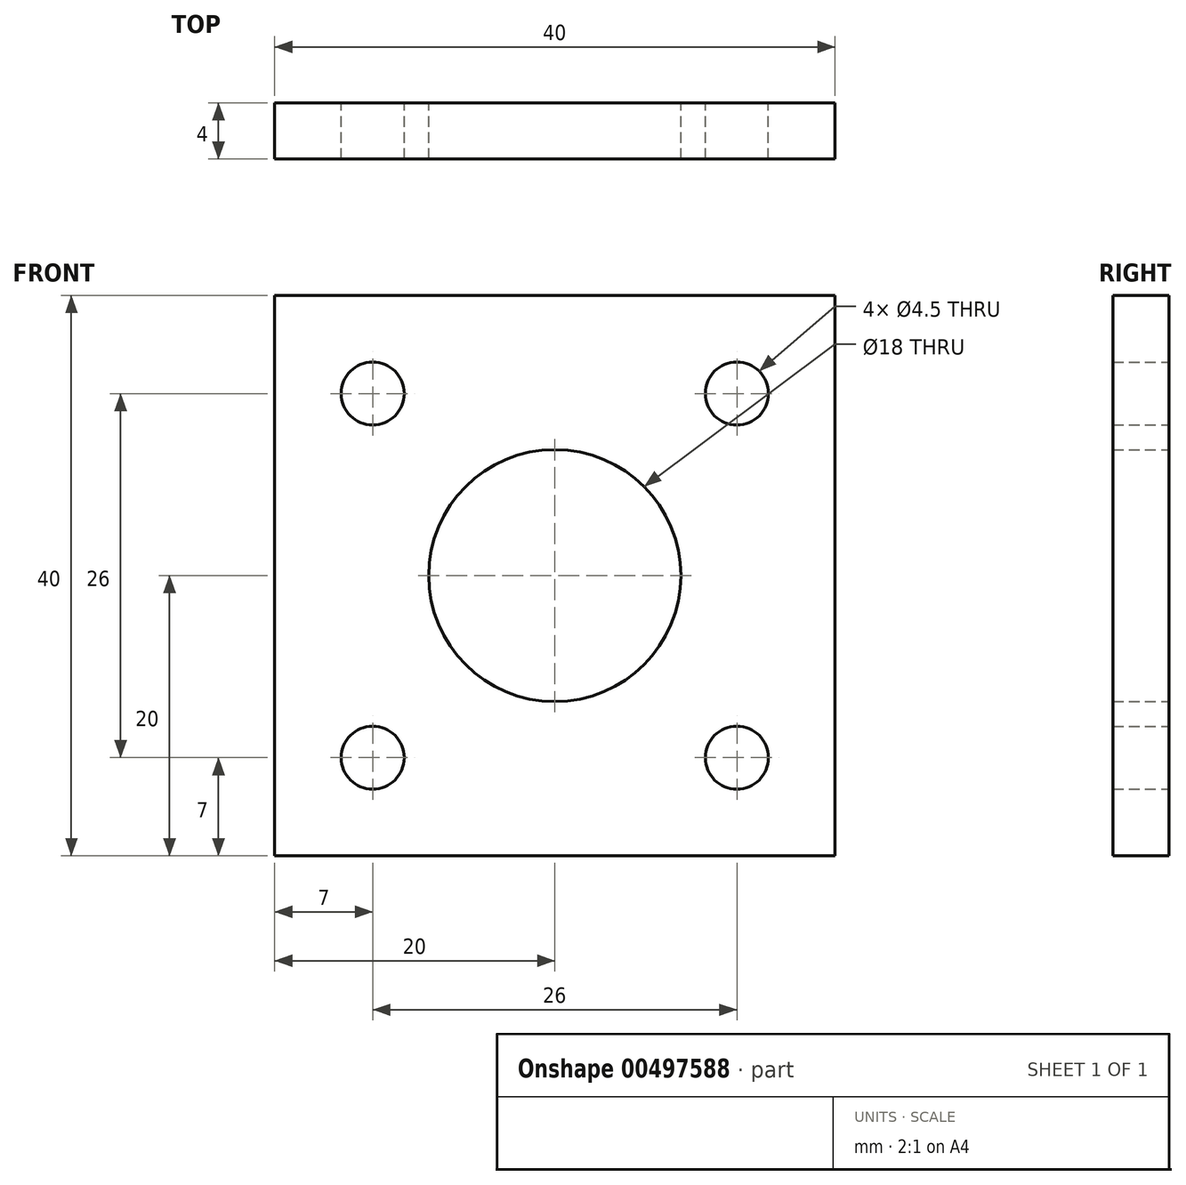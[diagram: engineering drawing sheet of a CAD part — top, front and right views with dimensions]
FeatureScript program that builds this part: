
annotation { "Feature Type Name" : "Feature", "Feature Type Description" : "" }
export const myFeature = defineFeature(function(context is Context, id is Id, definition is map)
    precondition{}
    {
        {
            var Q0;
            Q0=qCreatedBy(makeId("Front.planeOp"),FACE);
            var sketch = newSketch(context, id + "F0", { "sketchPlane" : qUnion([Q0])});
            skLineSegment(sketch, "E0.top", {"start": v(0, 0) * mm, "end": v(40, 0) * mm});
            skLineSegment(sketch, "E0.left", {"start": v(0, 40) * mm, "end": v(0, 0) * mm});
            skLineSegment(sketch, "E0.right", {"start": v(40, 40) * mm, "end": v(40, 0) * mm});
            skLineSegment(sketch, "E1", {"start": v(0, 40) * mm, "end": v(40, 40) * mm});
            skCircle(sketch, "E2", {"center": v(20, 20) * mm, "radius": 9 * mm});
            skCircle(sketch, "E3", {"center": v(7, 33) * mm, "radius": 2.25 * mm});
            skCircle(sketch, "E4", {"center": v(33, 33) * mm, "radius": 2.25 * mm});
            skCircle(sketch, "E5", {"center": v(33, 7) * mm, "radius": 2.25 * mm});
            skCircle(sketch, "E6", {"center": v(7, 7) * mm, "radius": 2.25 * mm});
            skCircle(sketch, "E7", {"center": v(20, 20) * mm, "radius": 11 * mm, "construction": true});
            skSolve(sketch);
        }
        {
            var Q0;
            Q0=makeQuery(id+"F0.imprint","IMPRINT",FACE,{"disambiguationData":[TD([[makeQuery(id+"F0.imprint","IMPRINT",EDGE,{"derivedFrom":sQuery(id+"F0.wireOp",EDGE,"E0.top")}),1.0]])]});
            extrude(context, id + "F1", {"entities" : qUnion([Q0]), "depth" : 4 * mm});
        }
    });
